# Revit family: 290022(2024)
name_source: partatom
category: Plumbing Fixtures
units: mm (PartAtom-declared; Revit-internal decimal feet)

## family parameters
Always vertical = Yes
Cut with Voids When Loaded = No
Maintain Annotation Orientation = No
OmniClass Number = 23.45.55.00
OmniClass Title = Sanitary Faucets, Wastes
Part Type = Normal
Room Calculation Point = No
Round Connector Dimension = Use Diameter
Shared = No
Work Plane-Based = No

## types (4) — shared parameters
3D View = https://static.oras.com
AssetType = Fixed
Backflow Prevention EN1717 = EB
BodyMaterial = Brass
Brand = Oras Group
Catalog Drawing URL = http://static.oras.com
Category B2B = Accessories
Category B2C = Shower solutions
Connection = Direct connection
Connection Size = G1/2
Dimension Drawing URL = http://static.oras.com
DurationUnit = Year
ETIM Class Number = EC011616 Parts for sanitary taps
FDV Document URL = http://www.oras.com
Finish = Polished
Group = Wall coupling for shower hose
IfcExportAs = IfcValveType
IfcExportType = FAUCET
Installation Type = Wall mounted
Installation and Maintenance Guide URL = http://static.oras.com
Interactive AR View URL = https://static.oras.com
Manufacturer = Oras Group
ManufacturerName = Oras Group
ManufacturerURL = http://www.oras group.com
Market = International;Finland;Norway;Sweden;Denmark;Poland;Estonia;Lithuania;Latvia;Germany;Austria;Belgium;Netherlands;Czech Republic;Italy
Material = Brass/Plastic
Max. Hot Water Supply = 80 °C
Mobile Product Information URL = http://mpi.oras.com
NBSDescription = Shower mixers
NBSReference = 45-35-70/335
NominalDepth = 58 mm
NominalHeight = 150 mm
NominalWidth = 75 mm
Product Family = Oras Group
Product Image URL = http://static.oras.com
Product URL = http://static.oras.com
Shape = Sculptured
Size = 150x100x150 mm
Technical DataSheet URL = http://www.oras.com
UNSPSC Class Number = 30181700 Faucets or taps
URL Declaration Of Performance (DOP) = http://static.oras.com
URL Declaration of Asbestos = http://static.oras.com
URL Declaration of Conformity = http://static.oras.com
URL Declaration of SCIP = http://static.oras.com
URL EU Packaging Declaration = http://static.oras.com
URL EcoLabel Declaration = http://static.oras.com
URL REACH = http://static.oras.com
Uniclass2 = Pr_40_30_96_78
Uniclass2015Description = Shower manual water supply sets
Uniclass2015Reference = Pr_40_20_87_78
Version = 1
VersionDate = 20/08/2024
Warranty Information URL = http://warranty.oras.com
WarrantyDescription = http://warranty.oras.com
WarrantyDurationUnit = Year
Working Pressure = 50 - 1000 kPa
zero-valued in all types: CloseOffRating, Default Elevation, FlowCoefficient

## per-type parameters (varying)
| type | BIMObjectName | Color | Color variants | FaucetMainMaterial | ModelReference | Product Code | Surface treatment | Type |
| 290022 Wall coupling for shower hose | 290022(2024) | Chrome | 290022-80;290022-81;290022-33 | Chrome | 290022 | 290022 | Chrome | 0 mm  [stored 0 ft] |
| 290022-33 Wall coupling for shower hose | 290022-33(2024) | Matt black |  | Matt black | 290022-33 | 290022-33 | Matt black | 33 mm  [stored 0.108268 ft] |
| 290022-80 Wall coupling for shower hose | 290022-80(2024) | Brushed steel |  | Brushed Steel | 290022-80 | 290022-80 | Brushed steel | 80 mm  [stored 0.262467 ft] |
| 290022-81 Wall coupling for shower hose | 290022-81(2024) | Brushed bronze |  | Brushed Bronze | 290022-81 | 290022-81 | Brushed bronze | 81 mm  [stored 0.265748 ft] |

note: column(s) folded — value = type name in every type: Model, Name, Name_en

note: [stored X ft] marks values corroborated as IEEE doubles in the binary element streams (Revit-internal decimal feet)

## geometry (parser evidence)
native form markers: Sweep x5
no freeform markers — native parametric forms only
